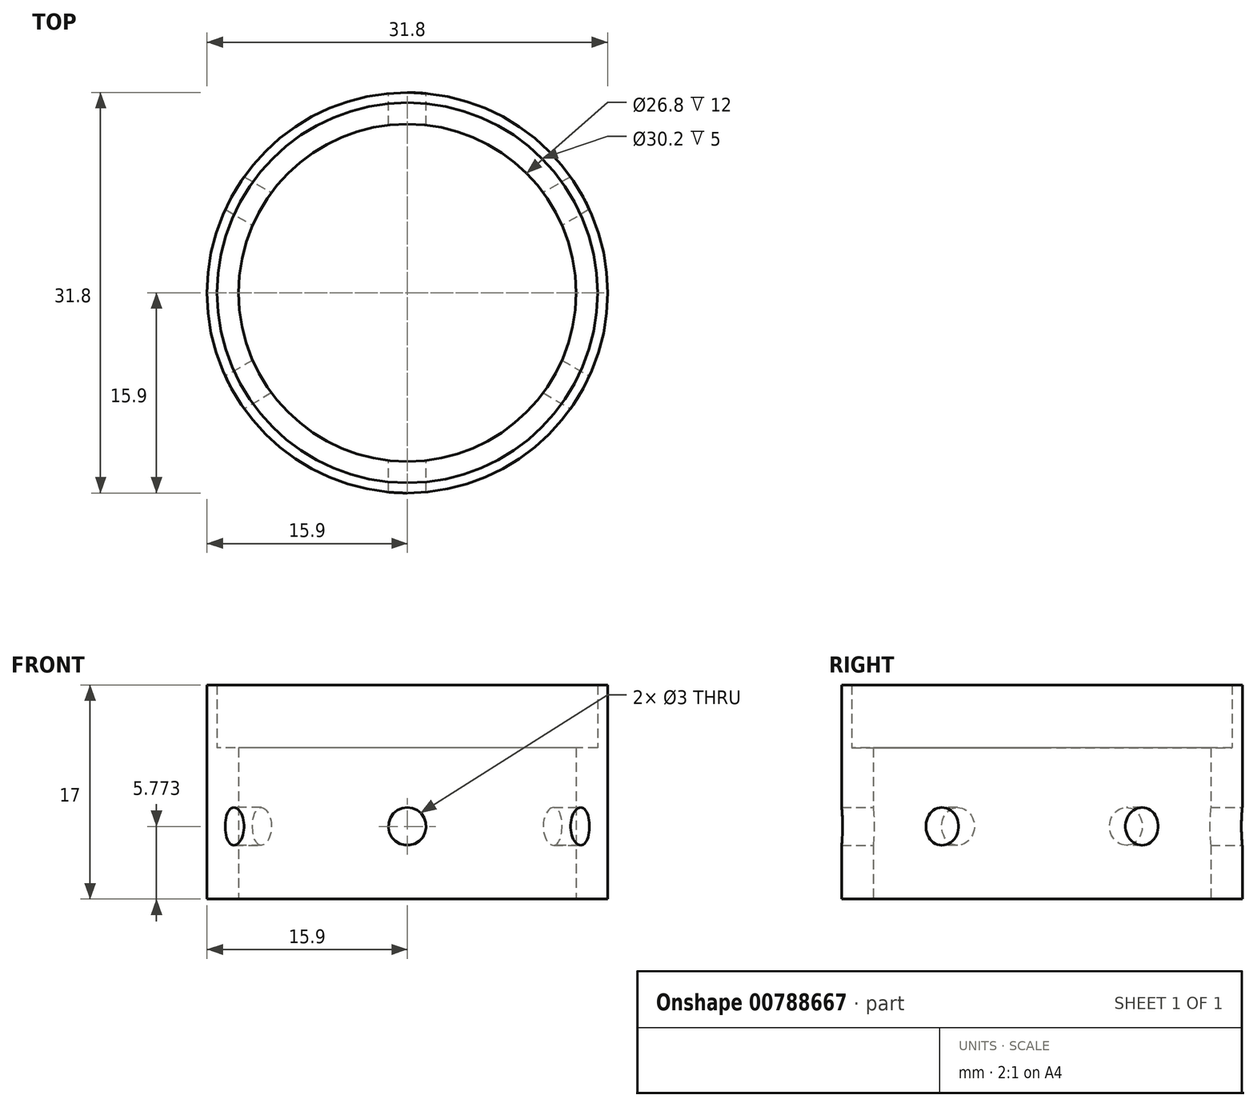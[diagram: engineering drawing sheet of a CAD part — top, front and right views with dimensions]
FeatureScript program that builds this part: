
annotation { "Feature Type Name" : "Feature", "Feature Type Description" : "" }
export const myFeature = defineFeature(function(context is Context, id is Id, definition is map)
    precondition{}
    {
        {
            var Q0;
            Q0=qCreatedBy(makeId("Top.planeOp"),FACE);
            var sketch = newSketch(context, id + "F0", { "sketchPlane" : qUnion([Q0])});
            skCircle(sketch, "E0", {"center": v(0, 0) * mm, "radius": 13.4 * mm});
            skCircle(sketch, "E1", {"center": v(0, 0) * mm, "radius": 15.9 * mm});
            skSolve(sketch);
        }
        {
            var Q0;
            Q0=makeQuery(id+"F0.imprint","IMPRINT",FACE,{"disambiguationData":[TD([[makeQuery(id+"F0.imprint","IMPRINT",EDGE,{"derivedFrom":sQuery(id+"F0.wireOp",EDGE,"E0")}),-1.0]])]});
            extrude(context, id + "F1", {"entities" : qUnion([Q0]), "depth" : 12 * mm, "offsetDistance" : 25 * mm});
        }
        {
            var Q0;
            Q0=qCreatedBy(makeId("Front.planeOp"),FACE);
            var sketch = newSketch(context, id + "F2", { "sketchPlane" : qUnion([Q0])});
            skCircle(sketch, "E2", {"center": v(0, 5.77) * mm, "radius": 1.5 * mm});
            skSolve(sketch);
        }
        {
            var Q0;
            Q0=makeQuery(id+"F2.imprint","IMPRINT",FACE,{"disambiguationData":[TD([[makeQuery(id+"F2.imprint","IMPRINT",EDGE,{"derivedFrom":sQuery(id+"F2.wireOp",EDGE,"E2")}),1.0]])]});
            extrude(context, id + "F3", {"entities" : qUnion([Q0]), "depth" : 50 * mm, "offsetDistance" : 25 * mm});
        }
        {
            var Q0;
            Q0=makeQuery(id+"F3.opExtrude","SWEPT_BODY",BODY,{"disambiguationData":[OSD([sQuery(id+"F2.wireOp",EDGE,"E2")])]});
            transform(context, id + "F4", {"entities" : qUnion([Q0]), "transformType" : TransformType.TRANSLATION_3D, "dx" : 0 * mm, "dy" : 25.2 * mm, "dz" : 0 * mm, "makeCopy" : false});
        }
        {
            var Q0;
            Q0=makeQuery(id+"F3.opExtrude","SWEPT_BODY",BODY,{"disambiguationData":[OSD([sQuery(id+"F2.wireOp",EDGE,"E2")])]});
            var Q1;
            Q1=makeQuery(id+"F1.opExtrude","SWEPT_FACE",FACE,{"disambiguationData":[OSD([sQuery(id+"F0.wireOp",EDGE,"E0")])]});
            circularPattern(context, id + "F5", {"entities" : qUnion([Q0]), "axis" : qUnion([Q1]), "angle" : 360 * degree, "instanceCount" : 3, "equalSpace" : true});
        }
        {
            var Q0;
            Q0=makeQuery(id+"F5.opPattern","COPY",BODY,{"derivedFrom":makeQuery(id+"F3.opExtrude","SWEPT_BODY",BODY,{"disambiguationData":[OSD([sQuery(id+"F2.wireOp",EDGE,"E2")])]}),"instanceName":"1"});
            var Q1;
            Q1=makeQuery(id+"F3.opExtrude","SWEPT_BODY",BODY,{"disambiguationData":[OSD([sQuery(id+"F2.wireOp",EDGE,"E2")])]});
            var Q2;
            Q2=makeQuery(id+"F5.opPattern","COPY",BODY,{"derivedFrom":makeQuery(id+"F3.opExtrude","SWEPT_BODY",BODY,{"disambiguationData":[OSD([sQuery(id+"F2.wireOp",EDGE,"E2")])]}),"instanceName":"2"});
            var Q3;
            Q3=makeQuery(id+"F1.opExtrude","SWEPT_BODY",BODY,{"disambiguationData":[OSD([sQuery(id+"F0.wireOp",EDGE,"E0"),sQuery(id+"F0.wireOp",EDGE,"E1")])]});
            booleanBodies(context, id + "F6", {"operationType" : BooleanOperationType.SUBTRACTION, "tools" : qUnion([Q0, Q1, Q2]), "targets" : qUnion([Q3])});
        }
        {
            var Q0;
            Q0=makeQuery(id+"F1.opExtrude","CAP_FACE",FACE,{"disambiguationData":[OSD([sQuery(id+"F0.wireOp",EDGE,"E0"),sQuery(id+"F0.wireOp",EDGE,"E1")])],"isStart":false});
            var sketch = newSketch(context, id + "F7", { "sketchPlane" : qUnion([Q0])});
            skCircle(sketch, "E3", {"center": v(0, 0) * mm, "radius": 15.9 * mm});
            skCircle(sketch, "E4", {"center": v(0, 0) * mm, "radius": 15.1 * mm});
            skSolve(sketch);
        }
        {
            var Q0;
            Q0=makeQuery(id+"F7.imprint","IMPRINT",FACE,{"disambiguationData":[TD([[makeQuery(id+"F7.imprint","IMPRINT",EDGE,{"derivedFrom":sQuery(id+"F7.wireOp",EDGE,"E3")}),1.0]])]});
            extrude(context, id + "F8", {"entities" : qUnion([Q0]), "operationType" : NewBodyOperationType.ADD, "depth" : 5 * mm, "offsetDistance" : 25 * mm});
        }
    });
